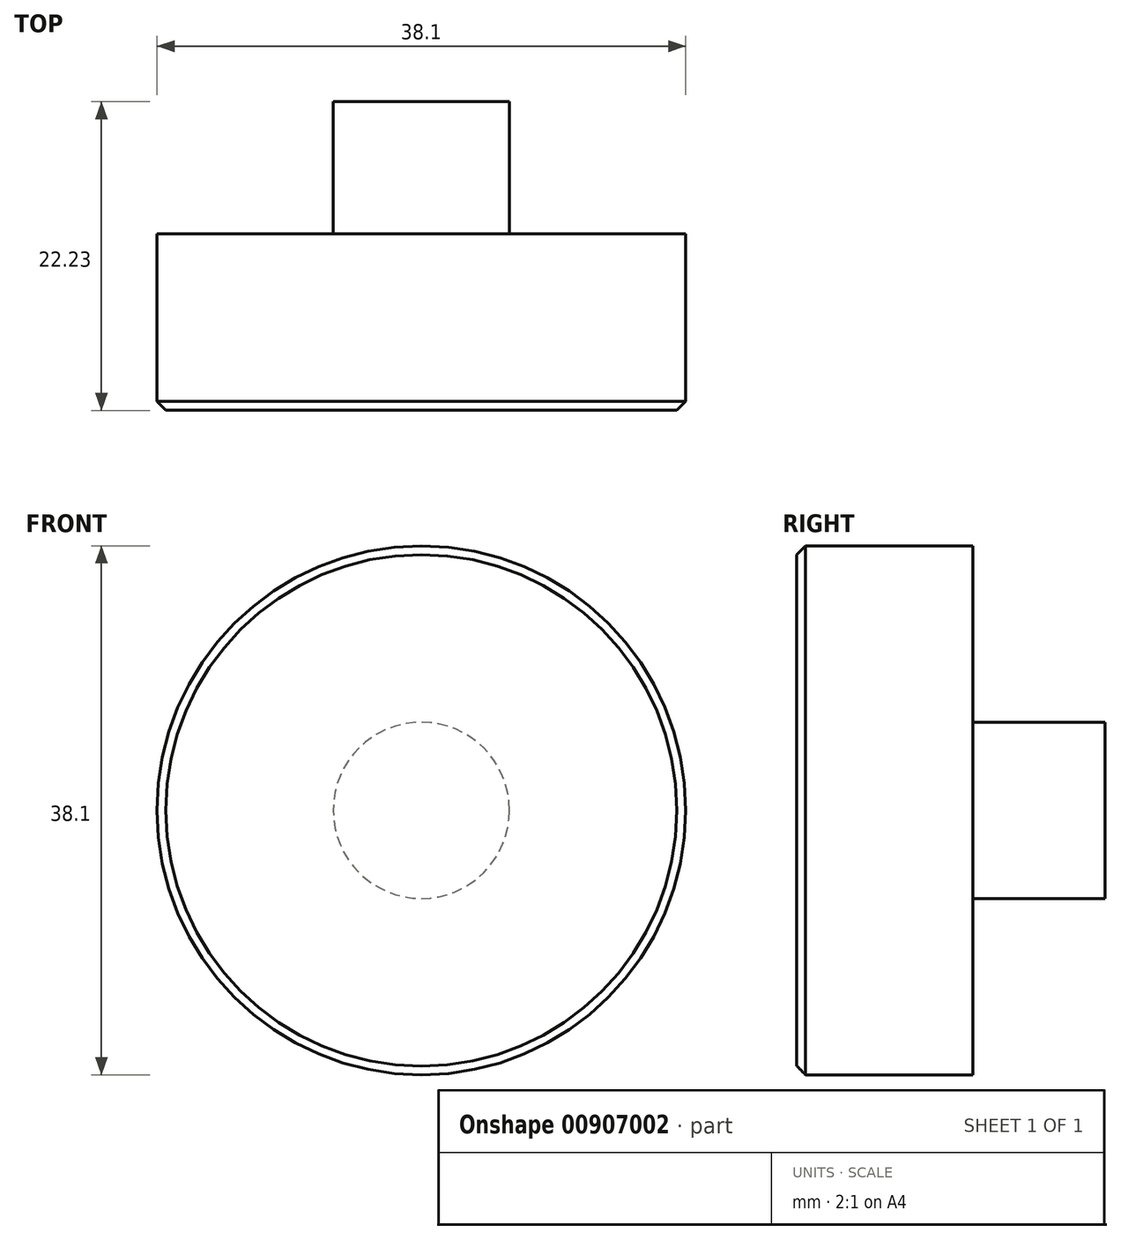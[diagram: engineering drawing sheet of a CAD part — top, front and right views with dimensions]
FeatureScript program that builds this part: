
annotation { "Feature Type Name" : "Feature", "Feature Type Description" : "" }
export const myFeature = defineFeature(function(context is Context, id is Id, definition is map)
    precondition{}
    {
        {
            var Q0;
            Q0=qCreatedBy(makeId("Front.planeOp"),FACE);
            var sketch = newSketch(context, id + "F0", { "sketchPlane" : qUnion([Q0])});
            skCircle(sketch, "E0", {"center": v(0, 0) * mm, "radius": 19.05 * mm});
            skSolve(sketch);
        }
        {
            var Q0;
            Q0=makeQuery(id+"F0.imprint","IMPRINT",FACE,{"disambiguationData":[TD([[makeQuery(id+"F0.imprint","IMPRINT",EDGE,{"derivedFrom":sQuery(id+"F0.wireOp",EDGE,"E0")}),1.0]])]});
            extrude(context, id + "F1", {"entities" : qUnion([Q0]), "depth" : 22.22 * mm, "offsetDistance" : 25.4 * mm});
        }
        {
            var Q0;
            Q0=makeQuery(id+"F1.opExtrude","CAP_FACE",FACE,{"disambiguationData":[OSD([sQuery(id+"F0.wireOp",EDGE,"E0")])],"isStart":true});
            var sketch = newSketch(context, id + "F2", { "sketchPlane" : qUnion([Q0])});
            skCircle(sketch, "E1", {"center": v(0, 0) * mm, "radius": 6.35 * mm});
            skSolve(sketch);
        }
        {
            var Q0;
            Q0=makeQuery(id+"F2.imprint","IMPRINT",FACE,{"disambiguationData":[TD([[makeQuery(id+"F2.imprint","IMPRINT",EDGE,{"derivedFrom":sQuery(id+"F2.wireOp",EDGE,"E1")}),-1.0]])]});
            extrude(context, id + "F3", {"entities" : qUnion([Q0]), "operationType" : NewBodyOperationType.REMOVE, "oppositeDirection" : true, "depth" : 9.52 * mm, "offsetDistance" : 25.4 * mm});
        }
        {
            var Q0;
            Q0=makeQuery(id+"F3.boolean.opBoolean","COPY",EDGE,{"derivedFrom":makeQuery(id+"F3.opExtrude","CAP_EDGE",EDGE,{"disambiguationData":[OSD([sQuery(id+"F2.wireOp",EDGE,"E1")])],"isStart":true})});
            var Q1;
            Q1=makeQuery(id+"F1.opExtrude","CAP_EDGE",EDGE,{"disambiguationData":[OSD([sQuery(id+"F0.wireOp",EDGE,"E0")])],"isStart":false});
            chamfer(context, id + "F4", {"entities" : qUnion([Q0, Q1]), "width" : 0.64 * mm, "tangentPropagation" : true});
        }
    });
